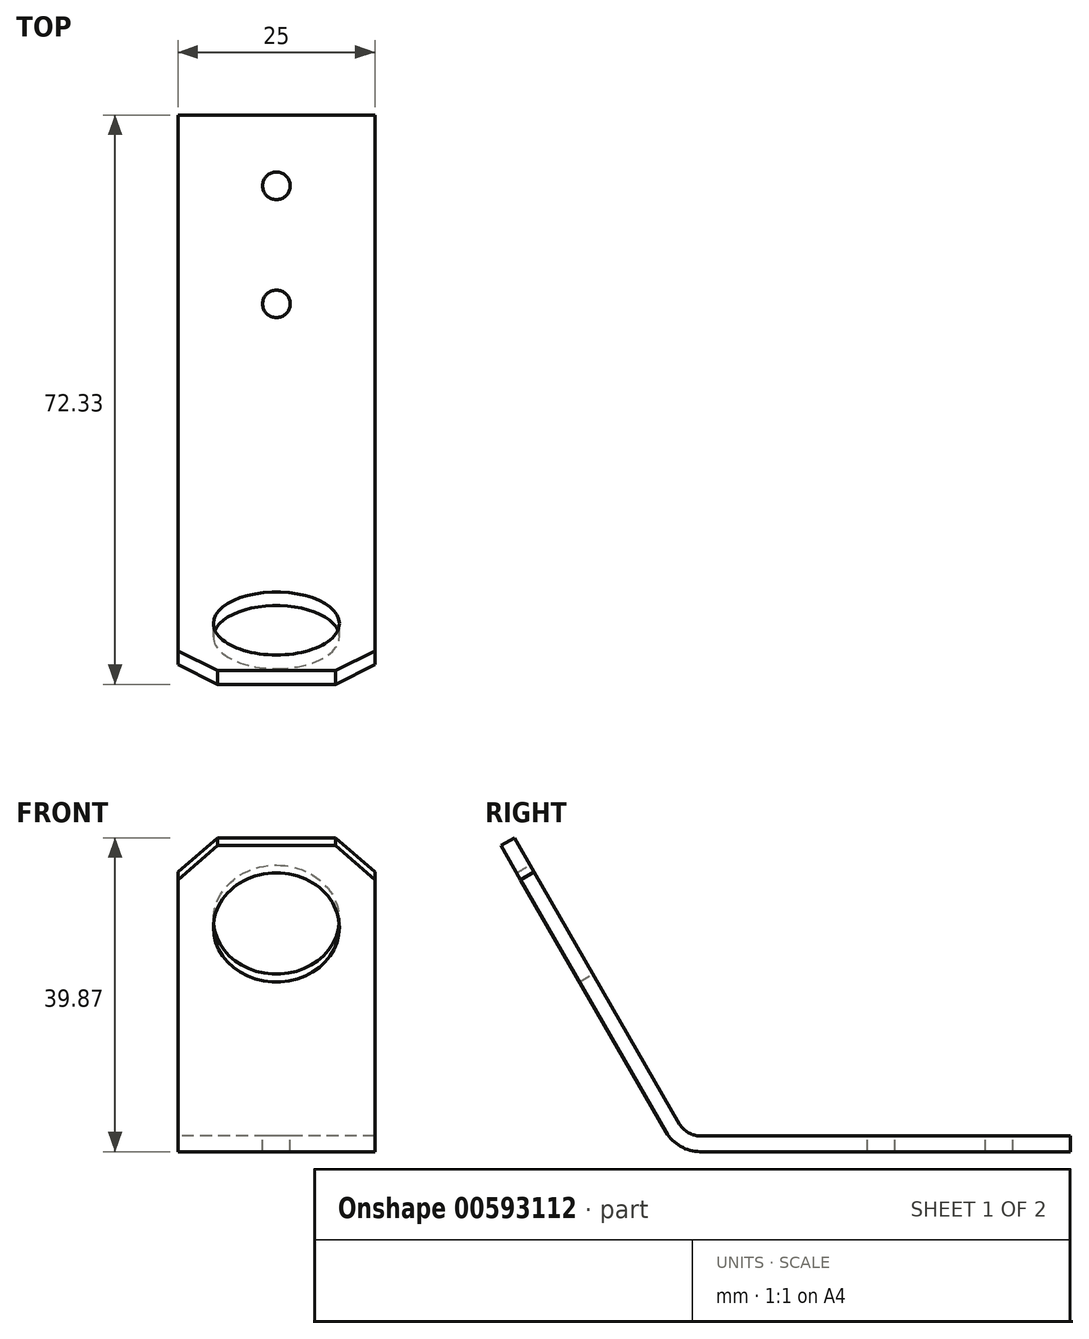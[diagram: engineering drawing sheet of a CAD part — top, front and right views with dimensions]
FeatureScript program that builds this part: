
annotation { "Feature Type Name" : "Feature", "Feature Type Description" : "" }
export const myFeature = defineFeature(function(context is Context, id is Id, definition is map)
    precondition{}
    {
        {
            var Q0;
            Q0=qCreatedBy(makeId("Right.planeOp"),FACE);
            var sketch = newSketch(context, id + "F0", { "sketchPlane" : qUnion([Q0])});
            skLineSegment(sketch, "E0", {"start": v(0, 41.9) * mm, "end": v(21, 5.53) * mm});
            skLineSegment(sketch, "E1", {"start": v(25.33, 3.03) * mm, "end": v(72.33, 3.03) * mm});
            skPoint(sketch, "E2.visualSharp", {"position": v(22.44, 3.03) * mm});
            skArc(sketch, "E2.filletArc", {"start": v(21, 5.53) * mm, "mid": v(22.83, 3.7) * mm, "end": v(25.33, 3.03) * mm});
            skLineSegment(sketch, "E3.0", {"start": v(25.33, 5.03) * mm, "end": v(72.33, 5.03) * mm});
            skArc(sketch, "E3.1", {"start": v(22.73, 6.53) * mm, "mid": v(23.83, 5.43) * mm, "end": v(25.33, 5.03) * mm});
            skLineSegment(sketch, "E3.2", {"start": v(1.73, 42.9) * mm, "end": v(22.73, 6.53) * mm});
            skLineSegment(sketch, "E4", {"start": v(72.33, 5.03) * mm, "end": v(72.33, 3.03) * mm});
            skLineSegment(sketch, "E5", {"start": v(0, 41.9) * mm, "end": v(1.73, 42.9) * mm});
            skSolve(sketch);
        }
        {
            var Q0;
            Q0=makeQuery(id+"F0.imprint","IMPRINT",FACE,{"disambiguationData":[TD([[makeQuery(id+"F0.imprint","IMPRINT",EDGE,{"derivedFrom":sQuery(id+"F0.wireOp",EDGE,"E0")}),1.0]])]});
            extrude(context, id + "F1", {"entities" : qUnion([Q0]), "depth" : 25 * mm, "offsetDistance" : 25 * mm});
        }
        {
            var Q0;
            Q0=makeQuery(id+"F1.opExtrude","SWEPT_FACE",FACE,{"disambiguationData":[OSD([sQuery(id+"F0.wireOp",EDGE,"E3.2")])]});
            var sketch = newSketch(context, id + "F2", { "sketchPlane" : qUnion([Q0])});
            skCircle(sketch, "E6", {"center": v(-12.5, 24.29) * mm, "radius": 8 * mm});
            skSolve(sketch);
        }
        {
            var Q0;
            Q0=qSketchRegion(id+"F2",true);
            extrude(context, id + "F3", {"entities" : qUnion([Q0]), "operationType" : NewBodyOperationType.REMOVE, "oppositeDirection" : true, "depth" : 25 * mm, "offsetDistance" : 25 * mm});
        }
        {
            var Q0;
            Q0=makeQuery(id+"F1.opExtrude","CAP_EDGE",EDGE,{"disambiguationData":[OSD([sQuery(id+"F0.wireOp",EDGE,"E5")])],"isStart":true});
            var Q1;
            Q1=makeQuery(id+"F1.opExtrude","CAP_EDGE",EDGE,{"disambiguationData":[OSD([sQuery(id+"F0.wireOp",EDGE,"E5")])],"isStart":false});
            chamfer(context, id + "F4", {"entities" : qUnion([Q0, Q1]), "width" : 5 * mm, "tangentPropagation" : true});
        }
        {
            var Q0;
            Q0=makeQuery(id+"F1.opExtrude","SWEPT_FACE",FACE,{"disambiguationData":[OSD([sQuery(id+"F0.wireOp",EDGE,"E3.0")])]});
            var sketch = newSketch(context, id + "F5", { "sketchPlane" : qUnion([Q0])});
            skCircle(sketch, "E7", {"center": v(12.5, 63.33) * mm, "radius": 1.75 * mm});
            skCircle(sketch, "E8", {"center": v(12.5, 48.33) * mm, "radius": 1.75 * mm});
            skSolve(sketch);
        }
        {
            var Q0;
            Q0=qSketchRegion(id+"F5",true);
            extrude(context, id + "F6", {"entities" : qUnion([Q0]), "operationType" : NewBodyOperationType.REMOVE, "oppositeDirection" : true, "depth" : 25 * mm, "offsetDistance" : 25 * mm});
        }
    });
